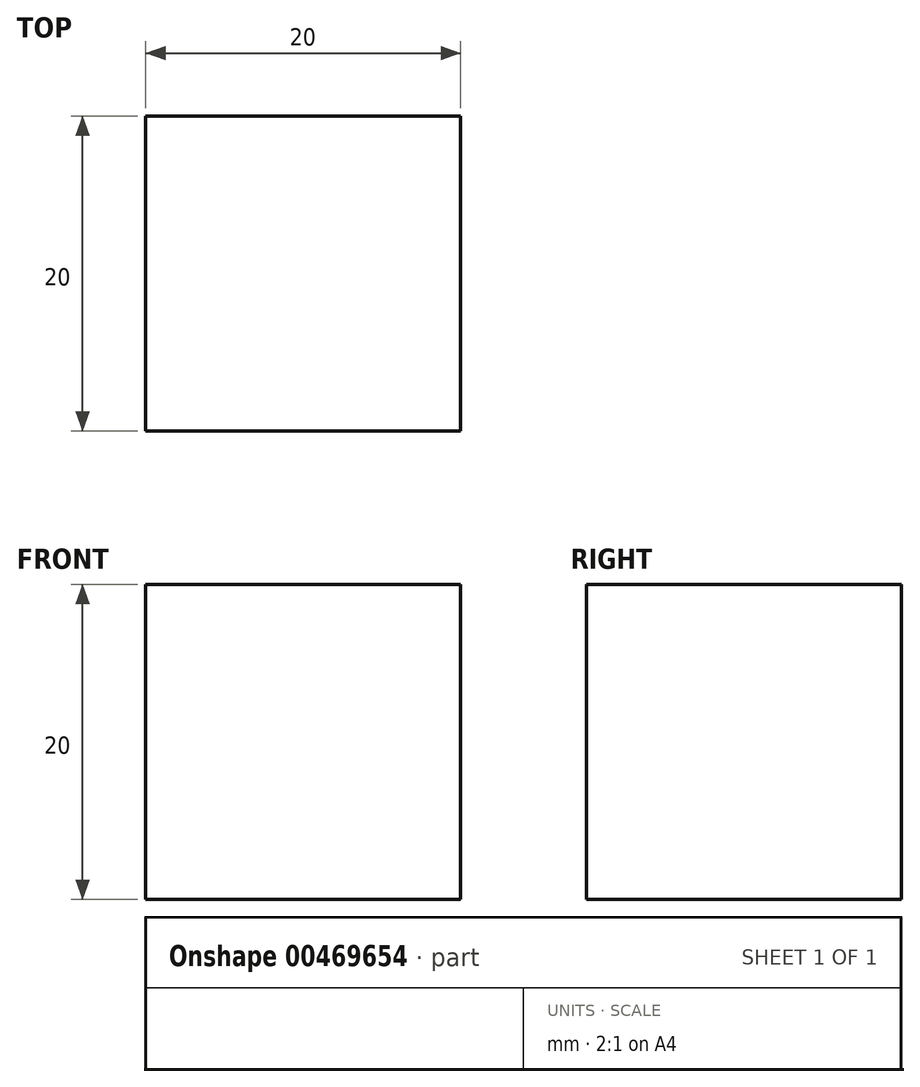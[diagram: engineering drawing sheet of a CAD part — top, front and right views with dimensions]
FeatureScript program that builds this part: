
annotation { "Feature Type Name" : "Feature", "Feature Type Description" : "" }
export const myFeature = defineFeature(function(context is Context, id is Id, definition is map)
    precondition{}
    {
        {
            var Q0;
            Q0=qCreatedBy(makeId("Front.planeOp"),FACE);
            var sketch = newSketch(context, id + "F0", { "sketchPlane" : qUnion([Q0])});
            skLineSegment(sketch, "E0.bottom", {"start": v(0, 0) * mm, "end": v(20, 0) * mm});
            skLineSegment(sketch, "E0.top", {"start": v(0, 20) * mm, "end": v(20, 20) * mm});
            skLineSegment(sketch, "E0.left", {"start": v(0, 0) * mm, "end": v(0, 20) * mm});
            skLineSegment(sketch, "E0.right", {"start": v(20, 0) * mm, "end": v(20, 20) * mm});
            skLineSegment(sketch, "E1.bottom", {"start": v(20, 5.96) * mm, "end": v(20, 5.96) * mm});
            skLineSegment(sketch, "E1.top", {"start": v(20, 0) * mm, "end": v(20, 0) * mm});
            skLineSegment(sketch, "E1.left", {"start": v(20, 5.96) * mm, "end": v(20, 0) * mm});
            skLineSegment(sketch, "E1.right", {"start": v(20, 5.96) * mm, "end": v(20, 0) * mm});
            skSolve(sketch);
        }
        {
            var Q0;
            Q0 = qSketchRegion(id + "F0", true);
            extrude(context, id + "F1", {"entities" : qUnion([Q0]), "depth" : 20 * mm});
        }
        {
            var Q0;
            Q0=makeQuery(id+"F1.opExtrude","CAP_FACE",FACE,{"disambiguationData":[OSD([sQuery(id+"F0.wireOp",EDGE,"E0.bottom"),sQuery(id+"F0.wireOp",EDGE,"E0.top"),sQuery(id+"F0.wireOp",EDGE,"E0.left"),sQuery(id+"F0.wireOp",EDGE,"E0.right"),sQuery(id+"F0.wireOp",EDGE,"E1.right")])],"isStart":false});
            var sketch = newSketch(context, id + "F2", { "sketchPlane" : qUnion([Q0])});
            skLineSegment(sketch, "E2", {"start": v(0, 20) * mm, "end": v(20, 0) * mm, "construction": true});
            skLineSegment(sketch, "E3", {"start": v(20, 0) * mm, "end": v(0, 0) * mm, "construction": true});
            skLineSegment(sketch, "E4", {"start": v(0, 0) * mm, "end": v(20, 20) * mm, "construction": true});
            skLineSegment(sketch, "E5", {"start": v(20, 20) * mm, "end": v(20, 10) * mm, "construction": true});
            skLineSegment(sketch, "E6", {"start": v(20, 10) * mm, "end": v(0, 10) * mm, "construction": true});
            skLineSegment(sketch, "E7", {"start": v(10, 20) * mm, "end": v(10, 0) * mm, "construction": true});
            skCircle(sketch, "E8", {"center": v(10, 10) * mm, "radius": 2.6 * mm});
            skCircle(sketch, "E9", {"center": v(5, 15) * mm, "radius": 2.6 * mm});
            skLineSegment(sketch, "E10.MirrorCS", {"start": v(10, 0) * mm, "end": v(10, 20) * mm, "construction": true});
            skSolve(sketch);
        }
    });
